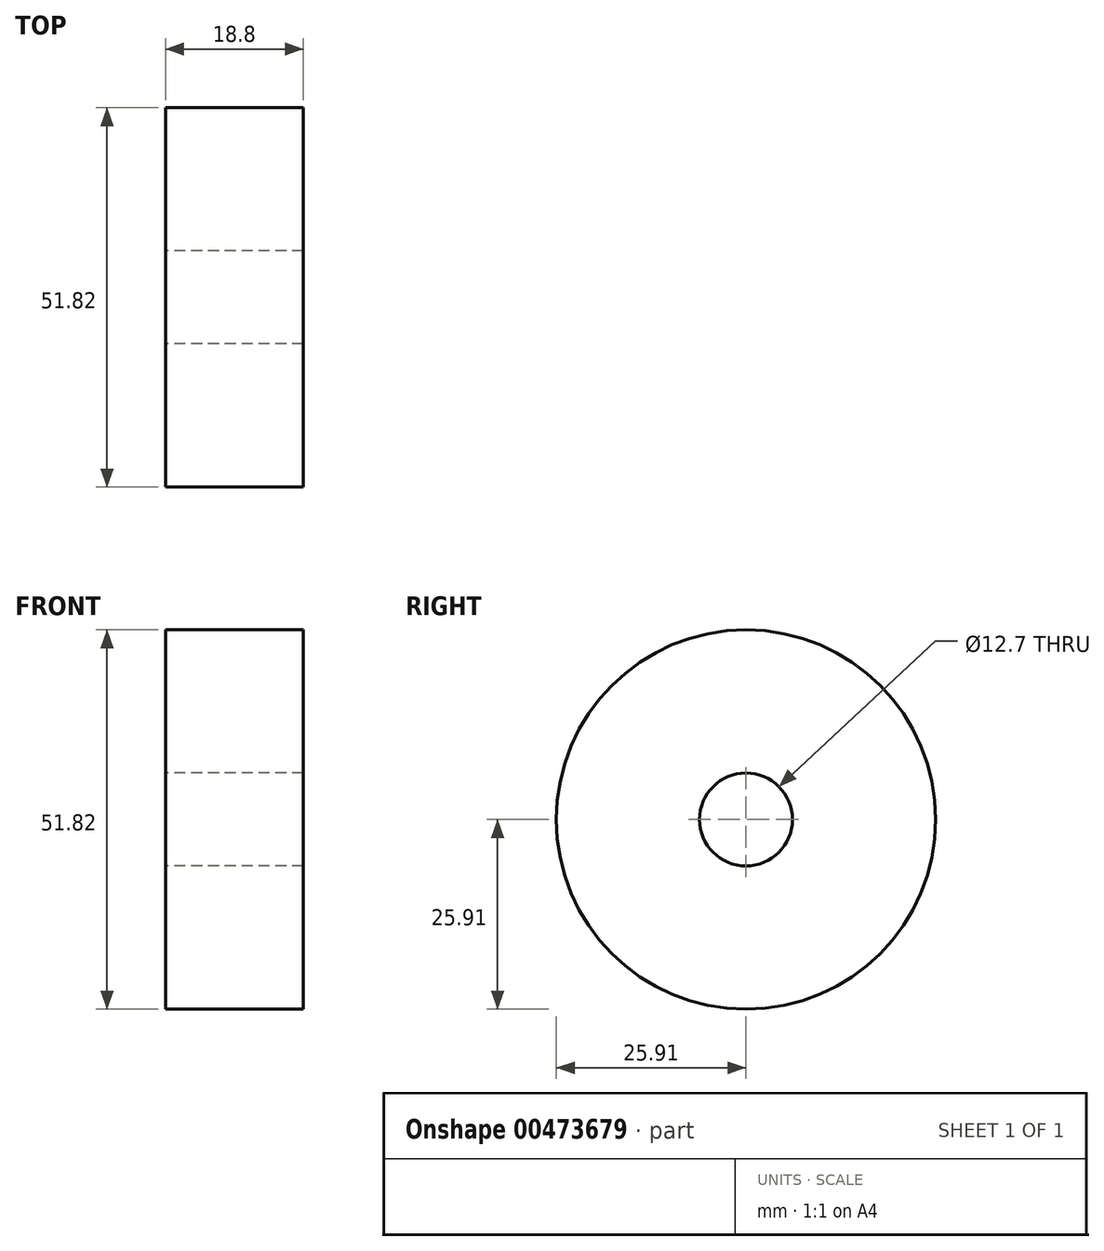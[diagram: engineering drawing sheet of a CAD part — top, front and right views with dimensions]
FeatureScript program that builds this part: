
annotation { "Feature Type Name" : "Feature", "Feature Type Description" : "" }
export const myFeature = defineFeature(function(context is Context, id is Id, definition is map)
    precondition{}
    {
        {
            var Q0;
            Q0=qCreatedBy(makeId("Right.planeOp"),FACE);
            var sketch = newSketch(context, id + "F0", { "sketchPlane" : qUnion([Q0])});
            skCircle(sketch, "E0", {"center": v(0, 0) * mm, "radius": 6.35 * mm});
            skCircle(sketch, "E1", {"center": v(0, 0) * mm, "radius": 25.9 * mm});
            skSolve(sketch);
        }
        {
            var Q0;
            Q0=makeQuery(id+"F0.imprint","IMPRINT",FACE,{"disambiguationData":[TD([[makeQuery(id+"F0.imprint","IMPRINT",EDGE,{"derivedFrom":sQuery(id+"F0.wireOp",EDGE,"E0")}),-1.0]])]});
            extrude(context, id + "F1", {"entities" : qUnion([Q0]), "depth" : 18.8 * mm, "offsetDistance" : 25.4 * mm});
        }
    });
